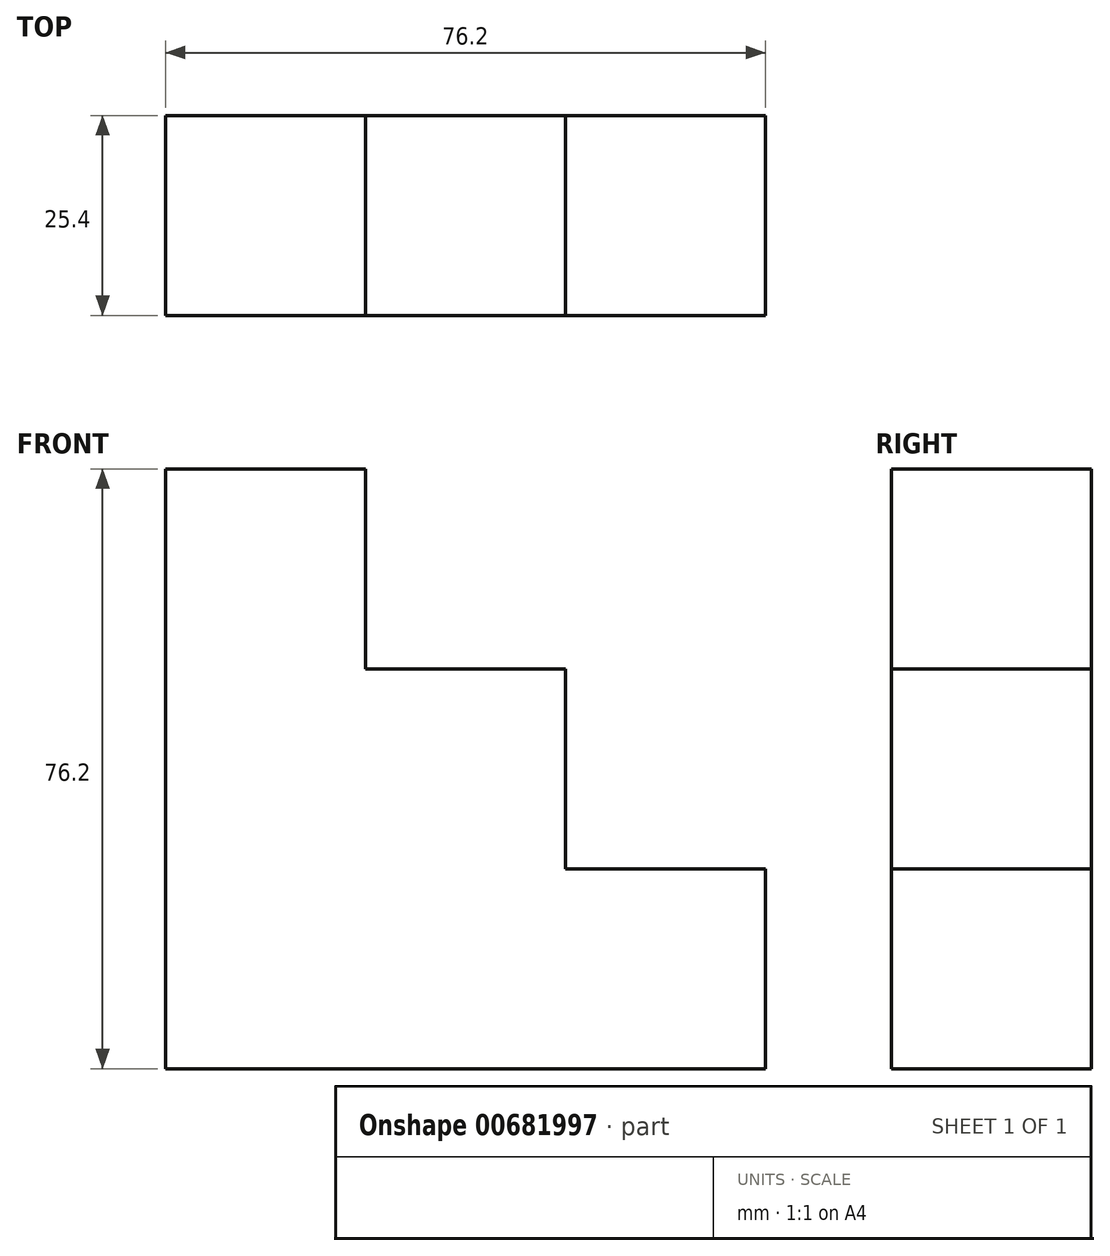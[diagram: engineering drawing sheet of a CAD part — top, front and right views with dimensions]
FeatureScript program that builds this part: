
annotation { "Feature Type Name" : "Feature", "Feature Type Description" : "" }
export const myFeature = defineFeature(function(context is Context, id is Id, definition is map)
    precondition{}
    {
        {
            var Q0;
            Q0=qCreatedBy(makeId("Front.planeOp"),FACE);
            var sketch = newSketch(context, id + "F0", { "sketchPlane" : qUnion([Q0])});
            skLineSegment(sketch, "E0", {"start": v(23.02, 0) * mm, "end": v(-53.18, 0) * mm});
            skLineSegment(sketch, "E1", {"start": v(-53.18, 0) * mm, "end": v(-53.18, 76.2) * mm});
            skLineSegment(sketch, "E2", {"start": v(-53.18, 76.2) * mm, "end": v(-27.78, 76.2) * mm});
            skLineSegment(sketch, "E3", {"start": v(-27.78, 76.2) * mm, "end": v(-27.78, 50.8) * mm});
            skLineSegment(sketch, "E4", {"start": v(-27.78, 50.8) * mm, "end": v(-2.38, 50.8) * mm});
            skLineSegment(sketch, "E5", {"start": v(-2.38, 50.8) * mm, "end": v(-2.38, 25.4) * mm});
            skLineSegment(sketch, "E6", {"start": v(-2.38, 25.4) * mm, "end": v(23.02, 25.4) * mm});
            skLineSegment(sketch, "E7", {"start": v(23.02, 25.4) * mm, "end": v(23.02, 0) * mm});
            skSolve(sketch);
        }
        {
            var Q0;
            Q0=makeQuery(id+"F0.imprint","IMPRINT",FACE,{"disambiguationData":[TD([[makeQuery(id+"F0.imprint","IMPRINT",EDGE,{"derivedFrom":sQuery(id+"F0.wireOp",EDGE,"E0")}),-1.0]])]});
            extrude(context, id + "F1", {"entities" : qUnion([Q0]), "depth" : 25.4 * mm, "offsetDistance" : 25.4 * mm});
        }
    });
